# Revit family: QF_ELECTROLUXPROFESSIONAL_1LSPHS_TD6-60SLD_E
name_source: partatom
category: Attrezzature speciali
units: mm (PartAtom-declared; Revit-internal decimal feet)

## family parameters
Basato su piano di lavoro = No
Condiviso = No
Punto di calcolo locali = No
Quota connettore circolare = Usa diametro
Sempre verticale = Sì
Taglio con vuoti quando caricato = No
Tipo di parte = Normale

## types (4) — shared parameters
ALL_MODEL_IMAGE = <Nessuno>
Cold Water Size = 0 mm
Compressed Air Pressure = 0.0 Pa
Compressed Air Size = 0 mm
Compressed Air Volume = 0.0 L/s
Condensate Return Size = 0 mm
Cycle = 50 Hz
Descrizione = TUMBLE DRYER DRUM VOLUME 1200L CAPACITY 60KG/132LB SLIDING DOOR
Direct Waste Size = 0 mm
Gas Size = 0 mm
Hot Water Size = 0 mm
Phase = 3
Produttore = Electrolux Professional
Steam Supply Maximum Pressure = 0.0 Pa
Steam Supply Minimum Pressure = 0.0 Pa
Steam Supply Size = 0 mm
URL = https://www.electroluxprofessional.com
Volts = 380 V
zero-valued in all types: Gas KW, Prospetto di default, Steam Pounds per Hour

## per-type parameters (varying)
| type | Depth Actual | Height Actual | Item Number | Length Actual | Watts | Weight in Pounds |
| 1L0HAF | 1495 mm  [stored 4.90486 ft] | 2550 mm  [stored 8.36614 ft] | 9875130038 | 1320 mm  [stored 4.33071 ft] | 62 W | 576 |
| 1L0HC4 | 1490 mm  [stored 4.88845 ft] | 2465 mm  [stored 8.08727 ft] | 9875130028 | 1314 mm  [stored 4.31102 ft] | 62 W | 524 |
| 1L0HCA | 1495 mm  [stored 4.90486 ft] | 2550 mm  [stored 8.36614 ft] | 9875130045 | 1320 mm  [stored 4.33071 ft] | 74 W | 576 |
| 1L0HDL | 1490 mm  [stored 4.88845 ft] | 2465 mm  [stored 8.08727 ft] | 9875130027 | 1314 mm  [stored 4.31102 ft] | 74 W | 524 |

note: [stored X ft] marks values corroborated as IEEE doubles in the binary element streams (Revit-internal decimal feet)

## geometry (parser evidence)
native form markers: Blend x2, Sweep x2
no freeform markers — native parametric forms only
